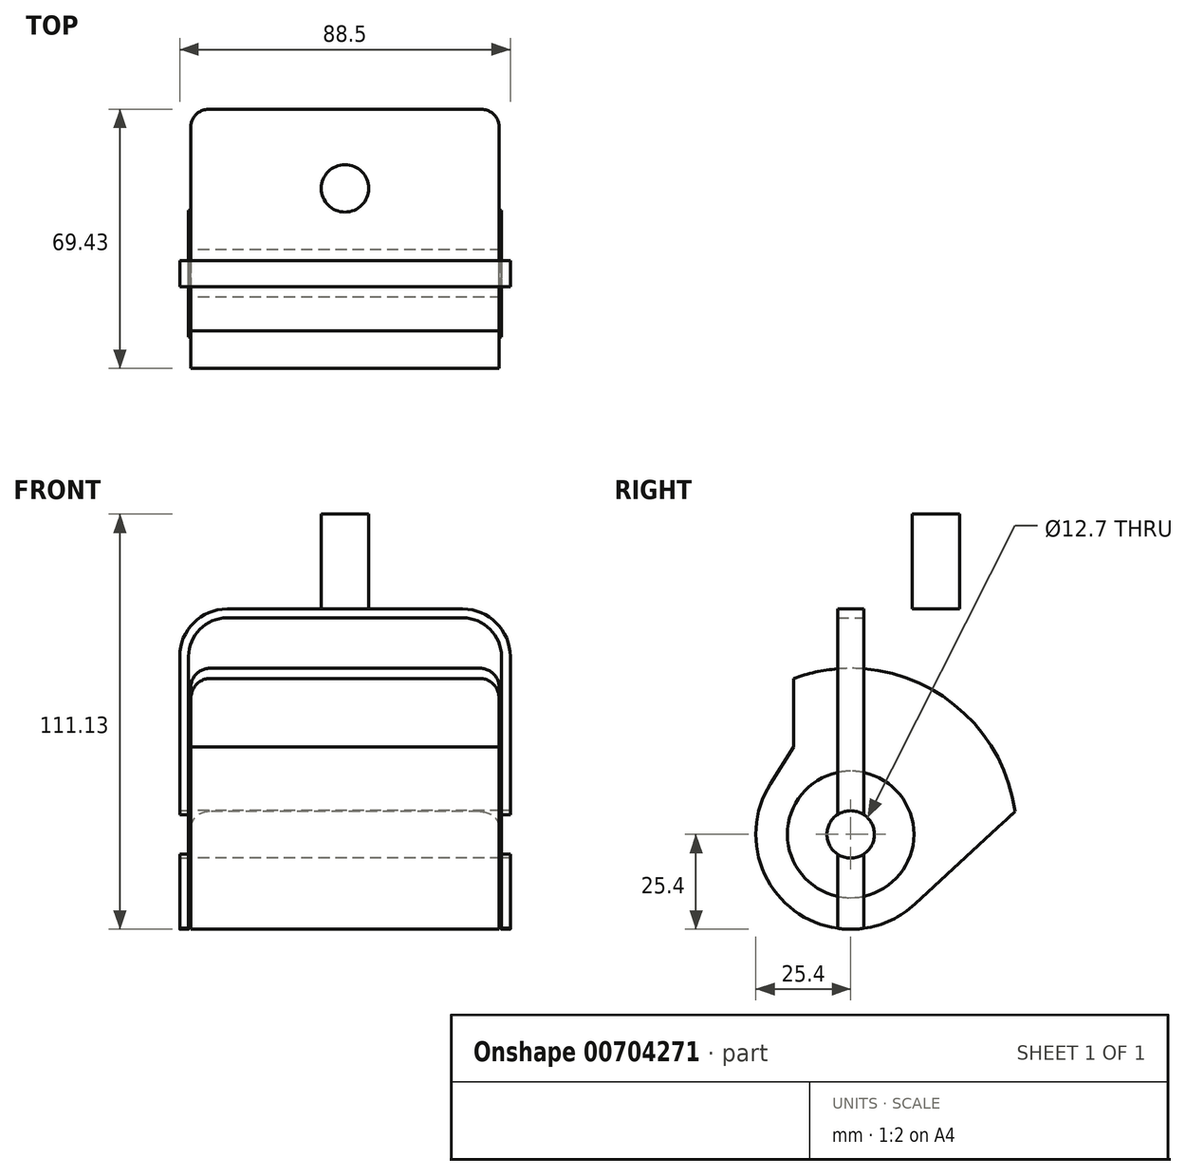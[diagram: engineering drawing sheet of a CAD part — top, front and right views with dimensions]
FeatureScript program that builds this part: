
annotation { "Feature Type Name" : "Feature", "Feature Type Description" : "" }
export const myFeature = defineFeature(function(context is Context, id is Id, definition is map)
    precondition{}
    {
        {
            assignVariable(context, id + "F0", {"name" : "mnt_hgt", "anyValue" : 4.12});
        }
        {
            assignVariable(context, id + "F1", {"name" : "wheel_dia", "anyValue" : 3.5});
        }
        {
            var Q0;
            Q0=qCreatedBy(makeId("Top.planeOp"),FACE);
            cPlane(context, id + "F2", {"entities" : qUnion([Q0]), "cplaneType" : CPlaneType.OFFSET, "offset" : (getVariable(context, 'mnt_hgt')) * mm, "width" : 152.4 * mm, "height" : 152.4 * mm});
        }
        {
            var Q0;
            Q0=qCreatedBy(makeId("Front.planeOp"),FACE);
            var sketch = newSketch(context, id + "F3", { "sketchPlane" : qUnion([Q0])});
            skLineSegment(sketch, "E0.bottom", {"start": v(0, 0) * mm, "end": v(41.28, 0) * mm});
            skLineSegment(sketch, "E0.top", {"start": v(0, 27.52) * mm, "end": v(41.28, 27.52) * mm});
            skLineSegment(sketch, "E0.right", {"start": v(41.28, 0) * mm, "end": v(41.28, 27.52) * mm});
            skLineSegment(sketch, "E1", {"start": v(-71.3, 44.45) * mm, "end": v(68.12, 44.45) * mm, "construction": true});
            skLineSegment(sketch, "E2.bottom", {"start": v(0, 38.1) * mm, "end": v(41.87, 38.1) * mm});
            skLineSegment(sketch, "E2.right", {"start": v(41.87, 38.1) * mm, "end": v(41.87, 27.52) * mm});
            skPoint(sketch, "E3", {"position": v(0, 27.52) * mm});
            skLineSegment(sketch, "E4", {"start": v(0, 0) * mm, "end": v(0, 38.1) * mm});
            skLineSegment(sketch, "E5.trimOffspring", {"start": v(0, 27.52) * mm, "end": v(41.87, 27.52) * mm});
            skLineSegment(sketch, "E6", {"start": v(0, 112.14) * mm, "end": v(0, 93.39) * mm, "construction": true});
            skSolve(sketch);
        }
        {
            var Q0;
            Q0=makeQuery(id+"F3.imprint","IMPRINT",FACE,{"disambiguationData":[TD([[makeQuery(id+"F3.imprint","IMPRINT",EDGE,{"derivedFrom":sQuery(id+"F3.wireOp",EDGE,"E2.bottom")}),-1.0]])]});
            var Q1;
            Q1=makeQuery(id+"F3.imprint","IMPRINT",FACE,{"disambiguationData":[TD([[makeQuery(id+"F3.imprint","IMPRINT",EDGE,{"derivedFrom":sQuery(id+"F3.wireOp",EDGE,"E0.bottom")}),1.0]])]});
            var Q2;
            Q2=sQuery(id+"F3.wireOp",EDGE,"E1");
            revolve(context, id + "F4", {"surfaceOperationType" : NewSurfaceOperationType.NEW, "entities" : qUnion([Q0, Q1]), "axis" : qUnion([Q2]), "revolveType" : RevolveType.FULL});
        }
        {
            var Q0;
            Q0=makeQuery(id+"F4.opRevolve","SWEPT_EDGE",EDGE,{"disambiguationData":[OSD([sQuery(id+"F3.wireOp",EDGE,"E0.bottom"),sQuery(id+"F3.wireOp",EDGE,"E0.right")])]});
            fillet(context, id + "F5", {"entities" : qUnion([Q0]), "radius" : 5.08 * mm, "tangentPropagation" : true, "allowEdgeOverflow" : false});
        }
        {
            var Q0;
            Q0=qCreatedBy(makeId("Front.planeOp"),FACE);
            var sketch = newSketch(context, id + "F6", { "sketchPlane" : qUnion([Q0])});
            skLineSegment(sketch, "E7", {"start": v(0, 104.78) * mm, "end": v(31.55, 104.78) * mm});
            skLineSegment(sketch, "E8", {"start": v(44.25, 92.08) * mm, "end": v(44.25, 19.05) * mm});
            skPoint(sketch, "E9.visualSharp", {"position": v(44.25, 104.78) * mm});
            skArc(sketch, "E9.filletArc", {"start": v(44.25, 92.08) * mm, "mid": v(40.53, 101.06) * mm, "end": v(31.55, 104.78) * mm});
            skLineSegment(sketch, "E10.0", {"start": v(41.9, 92.08) * mm, "end": v(41.9, 19.05) * mm});
            skArc(sketch, "E10.1", {"start": v(41.9, 92.08) * mm, "mid": v(38.86, 99.38) * mm, "end": v(31.55, 102.41) * mm});
            skLineSegment(sketch, "E10.2", {"start": v(0, 102.41) * mm, "end": v(31.55, 102.41) * mm});
            skLineSegment(sketch, "E11", {"start": v(0, 104.78) * mm, "end": v(0, 102.41) * mm});
            skLineSegment(sketch, "E12", {"start": v(41.9, 19.05) * mm, "end": v(44.25, 19.05) * mm});
            skSolve(sketch);
        }
        {
            var Q0;
            Q0=qSketchRegion(id+"F6",true);
            extrude(context, id + "F7", {"entities" : qUnion([Q0]), "endBound" : BoundingType.SYMMETRIC, "depth" : (2 * getVariable(context, 'wheel_dia')) * mm, "offsetDistance" : 25.4 * mm});
        }
        {
            var Q0;
            Q0=qCreatedBy(makeId("Right.planeOp"),FACE);
            var sketch = newSketch(context, id + "F8", { "sketchPlane" : qUnion([Q0])});
            skLineSegment(sketch, "E13", {"start": v(-15.3, 104.78) * mm, "end": v(-15.3, 67.82) * mm});
            skLineSegment(sketch, "E14", {"start": v(-15.3, 67.82) * mm, "end": v(-21.49, 58) * mm});
            skLineSegment(sketch, "E15", {"start": v(-46.04, 19.05) * mm, "end": v(9.95, 19.05) * mm, "construction": true});
            skLineSegment(sketch, "E16", {"start": v(9.95, 19.05) * mm, "end": v(17.25, 25.8) * mm, "construction": true});
            skLineSegment(sketch, "E17", {"start": v(60.9, 66.19) * mm, "end": v(60.9, 104.78) * mm});
            skLineSegment(sketch, "E18", {"start": v(60.9, 104.78) * mm, "end": v(-15.3, 104.78) * mm});
            skPoint(sketch, "E19", {"position": v(-18.05, 19.05) * mm});
            skCircle(sketch, "E20.0", {"center": v(0, 44.45) * mm, "radius": 6.35 * mm});
            skArc(sketch, "E21", {"start": v(-21.49, 58) * mm, "mid": v(-16.24, 24.92) * mm, "end": v(17.25, 25.8) * mm});
            skArc(sketch, "E22", {"start": v(17.25, 25.8) * mm, "mid": v(16.24, 63.98) * mm, "end": v(-21.49, 58) * mm, "construction": true});
            skLineSegment(sketch, "E23", {"start": v(-21.49, 58) * mm, "end": v(-46.04, 19.05) * mm, "construction": true});
            skLineSegment(sketch, "E24", {"start": v(17.25, 25.8) * mm, "end": v(60.9, 66.19) * mm});
            skSolve(sketch);
        }
        {
            var Q0;
            Q0=qSketchRegion(id+"F8",true);
            extrude(context, id + "F9", {"entities" : qUnion([Q0]), "operationType" : NewBodyOperationType.INTERSECT, "endBound" : BoundingType.THROUGH_ALL, "depth" : 25.4 * mm, "offsetDistance" : 25.4 * mm});
        }
        {
            var Q0;
            Q0=makeQuery(id+"F4.opRevolve","SWEPT_BODY",BODY,{"disambiguationData":[OSD([sQuery(id+"F3.wireOp",EDGE,"E0.bottom"),sQuery(id+"F3.wireOp",EDGE,"E0.right"),sQuery(id+"F3.wireOp",EDGE,"E2.bottom"),sQuery(id+"F3.wireOp",EDGE,"E2.right"),sQuery(id+"F3.wireOp",EDGE,"E4"),sQuery(id+"F3.wireOp",EDGE,"E5.trimOffspring")])]});
            var Q1;
            Q1=makeQuery(id+"F7.opExtrude","SWEPT_BODY",BODY,{"disambiguationData":[OSD([sQuery(id+"F6.wireOp",EDGE,"E7"),sQuery(id+"F6.wireOp",EDGE,"E8"),sQuery(id+"F6.wireOp",EDGE,"E9.filletArc"),sQuery(id+"F6.wireOp",EDGE,"E10.0"),sQuery(id+"F6.wireOp",EDGE,"E10.1"),sQuery(id+"F6.wireOp",EDGE,"E10.2"),sQuery(id+"F6.wireOp",EDGE,"E11"),sQuery(id+"F6.wireOp",EDGE,"E12")])]});
            var Q2;
            Q2=qCreatedBy(makeId("Right.planeOp"),FACE);
            mirror(context, id + "F10", {"operationType" : NewBodyOperationType.ADD, "entities" : qUnion([Q0, Q1]), "mirrorPlane" : qUnion([Q2])});
        }
        {
            var Q0;
            {var subQ0=makeQuery(id+"F7.opExtrude","SWEPT_FACE",FACE,{"disambiguationData":[OSD([sQuery(id+"F6.wireOp",EDGE,"E7")])]});Q0=makeQuery(id+"F10.boolean.opBoolean","MERGE",FACE,{"derivedFrom":[subQ0,makeQuery(id+"F10.opPattern","COPY",FACE,{"derivedFrom":subQ0,"instanceName":"1"})]});}
            var sketch = newSketch(context, id + "F11", { "sketchPlane" : qUnion([Q0])});
            skCircle(sketch, "E25", {"center": v(0, 22.8) * mm, "radius": 6.35 * mm});
            skSolve(sketch);
        }
        {
            var Q0;
            Q0=qSketchRegion(id+"F11",true);
            extrude(context, id + "F12", {"entities" : qUnion([Q0]), "operationType" : NewBodyOperationType.ADD, "depth" : 25.4 * mm, "offsetDistance" : 25.4 * mm});
        }
    });
